# Revit family: Adaptor 4 MTP
name_source: partatom
category: Installations électriques
units: mm (PartAtom-declared; Revit-internal decimal feet)

## family parameters
Basée sur le plan de construction = Non
Conserver l'orientation des annotations = Non
Cote de connecteur circulaire = Utiliser le diamètre
Couper avec des vides une fois chargée = Non
Partagée = Non
Point de calcul de pièce = Non
Toujours verticalement = Oui
Type d'élément = Normal

## types (2) — shared parameters
Color = IDS_NOIR
Depth = 44.7 mm
E-catalogue link = https://www.legrand.fr
ETIM class = EC001130
Function = Patch panels with optical connector Legrand
Height = 23 mm  [stored 0.0754593 ft]
Height of the connectors = 10 mm  [stored 0.0328084 ft]
IK = IK04
IP = IP20
Number of connectors = 4
Opening height = 6.5 mm
Opening width = 8.35 mm  [stored 0.027395 ft]
Operating temperature = -10°C à 60°C
RAL Number = 9017
Storage temperature = -10°C à 60°C
Type of connector external = MT_MPO
Type of connector interior = MT_MPO
Width (mm) = 108.8 mm
Width of the connectors = 13.5 mm  [stored 0.0442913 ft]
zero-valued in all types: Elévation par défaut

## per-type parameters (varying)
| type | Colour of the connectors | EAN | Fiber optic type | Legrand part number |
| Adaptor 4 MTP single mode | IDS_VERT | 3414970962041 | Single mode | 032133 |
| Adaptor 4 MTP multimode | IDS_JAUNE | 3414970962065 | Multimode | 032134 |

note: column(s) folded — value = type name in every type: BIM wording

note: [stored X ft] marks values corroborated as IEEE doubles in the binary element streams (Revit-internal decimal feet)
